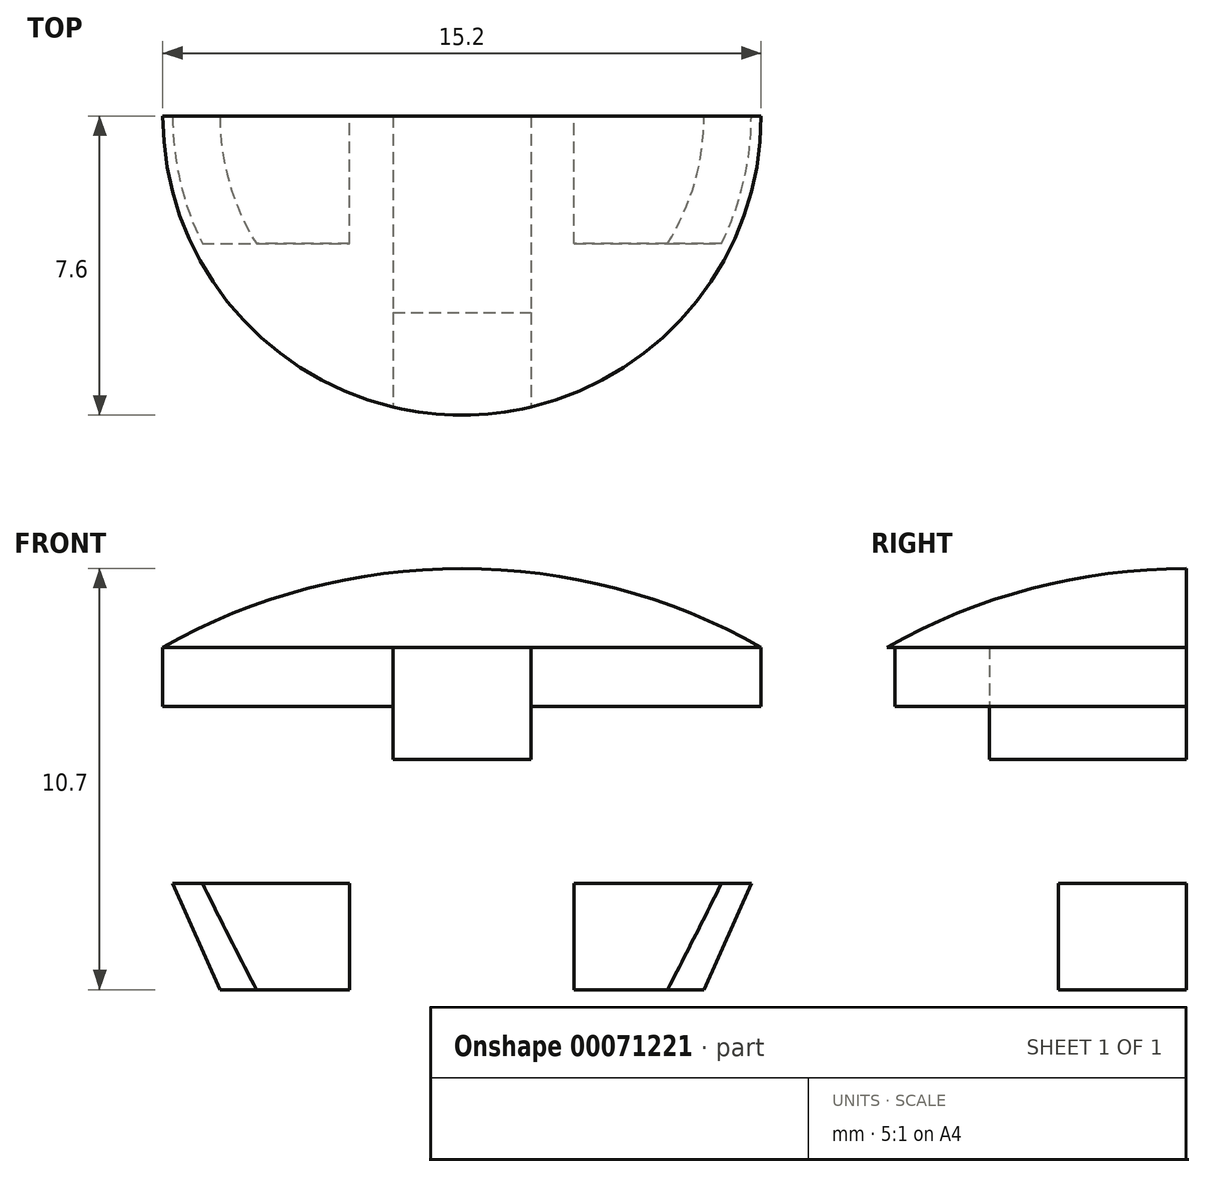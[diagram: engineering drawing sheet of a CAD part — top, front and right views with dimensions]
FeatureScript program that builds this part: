
annotation { "Feature Type Name" : "Feature", "Feature Type Description" : "" }
export const myFeature = defineFeature(function(context is Context, id is Id, definition is map)
    precondition{}
    {
        {
            var Q0;
            Q0=qCreatedBy(makeId("Front.planeOp"),FACE);
            var sketch = newSketch(context, id + "F0", { "sketchPlane" : qUnion([Q0])});
            skLineSegment(sketch, "E0", {"start": v(-7.6, 0) * mm, "end": v(7.6, 0) * mm});
            skLineSegment(sketch, "E1", {"start": v(0, 0) * mm, "end": v(0, 2) * mm});
            skArc(sketch, "E2", {"start": v(7.6, 0) * mm, "mid": v(0, 2) * mm, "end": v(-7.6, 0) * mm});
            skLineSegment(sketch, "E3.top", {"start": v(-7.6, -1.5) * mm, "end": v(7.6, -1.5) * mm});
            skLineSegment(sketch, "E3.left", {"start": v(-7.6, 0) * mm, "end": v(-7.6, -1.5) * mm});
            skLineSegment(sketch, "E3.right", {"start": v(7.6, 0) * mm, "end": v(7.6, -1.5) * mm});
            skLineSegment(sketch, "E4", {"start": v(0, 0) * mm, "end": v(0, -1.5) * mm});
            skLineSegment(sketch, "E5.bottom", {"start": v(-1.75, 0) * mm, "end": v(1.75, 0) * mm});
            skLineSegment(sketch, "E5.top", {"start": v(-1.75, -2.85) * mm, "end": v(1.75, -2.85) * mm});
            skLineSegment(sketch, "E5.left", {"start": v(-1.75, 0) * mm, "end": v(-1.75, -2.85) * mm});
            skLineSegment(sketch, "E5.right", {"start": v(1.75, 0) * mm, "end": v(1.75, -2.85) * mm});
            skLineSegment(sketch, "E6.bottom", {"start": v(2.85, -1.5) * mm, "end": v(5.1, -1.5) * mm});
            skLineSegment(sketch, "E6.top", {"start": v(2.85, -8.7) * mm, "end": v(5.1, -8.7) * mm});
            skLineSegment(sketch, "E6.left", {"start": v(2.85, -1.5) * mm, "end": v(2.85, -8.7) * mm});
            skLineSegment(sketch, "E6.right", {"start": v(5.1, -1.5) * mm, "end": v(5.1, -8.7) * mm});
            skLineSegment(sketch, "E7", {"start": v(5.1, -6) * mm, "end": v(7.35, -6) * mm});
            skLineSegment(sketch, "E8", {"start": v(7.35, -6) * mm, "end": v(6.15, -8.7) * mm});
            skLineSegment(sketch, "E9", {"start": v(6.15, -8.7) * mm, "end": v(5.1, -8.7) * mm});
            skLineSegment(sketch, "E10.MirrorCS", {"start": v(-2.85, -1.5) * mm, "end": v(-5.1, -1.5) * mm});
            skLineSegment(sketch, "E11.MirrorCS", {"start": v(-2.85, -1.5) * mm, "end": v(-2.85, -8.7) * mm});
            skLineSegment(sketch, "E12.MirrorCS", {"start": v(-5.1, -1.5) * mm, "end": v(-5.1, -8.7) * mm});
            skLineSegment(sketch, "E13.MirrorCS", {"start": v(-2.85, -8.7) * mm, "end": v(-5.1, -8.7) * mm});
            skLineSegment(sketch, "E14.MirrorCS", {"start": v(-6.15, -8.7) * mm, "end": v(-5.1, -8.7) * mm});
            skLineSegment(sketch, "E15.MirrorCS", {"start": v(-7.35, -6) * mm, "end": v(-6.15, -8.7) * mm});
            skLineSegment(sketch, "E16.MirrorCS", {"start": v(-5.1, -6) * mm, "end": v(-7.35, -6) * mm});
            skLineSegment(sketch, "E17", {"start": v(5.1, -6) * mm, "end": v(2.85, -6) * mm});
            skLineSegment(sketch, "E18.MirrorCS", {"start": v(-5.1, -6) * mm, "end": v(-2.85, -6) * mm});
            skSolve(sketch);
        }
        {
            var Q0;
            {var subQ0=sQuery(id+"F0.wireOp",EDGE,"E3.left");Q0=makeQuery(id+"F0.imprint","IMPRINT",FACE,{"disambiguationData":[TD([[makeQuery(id+"F0.imprint","IMPRINT",EDGE,{"derivedFrom":subQ0}),1.0]])]});}
            var Q1;
            {var subQ0=sQuery(id+"F0.wireOp",EDGE,"E1");Q1=makeQuery(id+"F0.imprint","IMPRINT",FACE,{"disambiguationData":[TD([[makeQuery(id+"F0.imprint","IMPRINT",EDGE,{"derivedFrom":subQ0}),1.0]])]});}
            var Q2;
            {var subQ0=sQuery(id+"F0.wireOp",EDGE,"E4");Q2=makeQuery(id+"F0.imprint","IMPRINT",FACE,{"disambiguationData":[TD([[makeQuery(id+"F0.imprint","IMPRINT",EDGE,{"derivedFrom":subQ0}),-1.0]])]});}
            var Q3;
            Q3=sQuery(id+"F0.wireOp",EDGE,"E1");
            revolve(context, id + "F1", {"entities" : qUnion([Q0, Q1, Q2]), "axis" : qUnion([Q3]), "revolveType" : RevolveType.FULL});
        }
        {
            var Q0;
            {var subQ0=sQuery(id+"F0.wireOp",EDGE,"E10.MirrorCS");Q0=makeQuery(id+"F0.imprint","IMPRINT",FACE,{"disambiguationData":[TD([[makeQuery(id+"F0.imprint","IMPRINT",EDGE,{"derivedFrom":subQ0}),1.0]])]});}
            var Q1;
            {var subQ0=sQuery(id+"F0.wireOp",EDGE,"E13.MirrorCS");Q1=makeQuery(id+"F0.imprint","IMPRINT",FACE,{"disambiguationData":[TD([[makeQuery(id+"F0.imprint","IMPRINT",EDGE,{"derivedFrom":subQ0}),-1.0]])]});}
            var Q2;
            {var subQ0=sQuery(id+"F0.wireOp",EDGE,"E6.top");Q2=makeQuery(id+"F0.imprint","IMPRINT",FACE,{"disambiguationData":[TD([[makeQuery(id+"F0.imprint","IMPRINT",EDGE,{"derivedFrom":subQ0}),1.0]])]});}
            var Q3;
            {var subQ0=sQuery(id+"F0.wireOp",EDGE,"E6.bottom");Q3=makeQuery(id+"F0.imprint","IMPRINT",FACE,{"disambiguationData":[TD([[makeQuery(id+"F0.imprint","IMPRINT",EDGE,{"derivedFrom":subQ0}),-1.0]])]});}
            extrude(context, id + "F2", {"entities" : qUnion([Q0, Q1, Q2, Q3]), "operationType" : NewBodyOperationType.ADD, "endBound" : BoundingType.SYMMETRIC, "depth" : 6.5 * mm});
        }
        {
            var Q0;
            {var subQ0=sQuery(id+"F0.wireOp",EDGE,"E14.MirrorCS");Q0=makeQuery(id+"F0.imprint","IMPRINT",FACE,{"disambiguationData":[TD([[makeQuery(id+"F0.imprint","IMPRINT",EDGE,{"derivedFrom":subQ0}),1.0]])]});}
            var Q1;
            {var subQ2=sQuery(id+"F0.wireOp",EDGE,"E7");Q1=makeQuery(id+"F0.imprint","IMPRINT",FACE,{"disambiguationData":[TD([[makeQuery(id+"F0.imprint","IMPRINT",EDGE,{"derivedFrom":subQ2}),-1.0]])]});}
            var Q2;
            Q2=sQuery(id+"F0.wireOp",EDGE,"E1");
            revolve(context, id + "F3", {"operationType" : NewBodyOperationType.ADD, "entities" : qUnion([Q0, Q1]), "axis" : qUnion([Q2]), "revolveType" : RevolveType.SYMMETRIC, "angle" : 70 * degree});
        }
        {
            var Q0;
            {var subQ0=sQuery(id+"F0.wireOp",EDGE,"E4");Q0=makeQuery(id+"F0.imprint","IMPRINT",FACE,{"disambiguationData":[TD([[makeQuery(id+"F0.imprint","IMPRINT",EDGE,{"derivedFrom":subQ0}),-1.0]])]});}
            var Q1;
            {var subQ0=sQuery(id+"F0.wireOp",EDGE,"E4");Q1=makeQuery(id+"F0.imprint","IMPRINT",FACE,{"disambiguationData":[TD([[makeQuery(id+"F0.imprint","IMPRINT",EDGE,{"derivedFrom":subQ0}),1.0]])]});}
            extrude(context, id + "F4", {"entities" : qUnion([Q0, Q1]), "operationType" : NewBodyOperationType.REMOVE, "endBound" : BoundingType.SYMMETRIC, "oppositeDirection" : true, "depth" : 25 * mm});
        }
        {
            var Q0;
            {var subQ1=sQuery(id+"F0.wireOp",EDGE,"E5.top");Q0=makeQuery(id+"F0.imprint","IMPRINT",FACE,{"disambiguationData":[TD([[makeQuery(id+"F0.imprint","IMPRINT",EDGE,{"derivedFrom":subQ1}),1.0]])]});}
            var Q1;
            {var subQ0=sQuery(id+"F0.wireOp",EDGE,"E4");Q1=makeQuery(id+"F0.imprint","IMPRINT",FACE,{"disambiguationData":[TD([[makeQuery(id+"F0.imprint","IMPRINT",EDGE,{"derivedFrom":subQ0}),-1.0]])]});}
            var Q2;
            {var subQ0=sQuery(id+"F0.wireOp",EDGE,"E4");Q2=makeQuery(id+"F0.imprint","IMPRINT",FACE,{"disambiguationData":[TD([[makeQuery(id+"F0.imprint","IMPRINT",EDGE,{"derivedFrom":subQ0}),1.0]])]});}
            extrude(context, id + "F5", {"entities" : qUnion([Q0, Q1, Q2]), "operationType" : NewBodyOperationType.ADD, "endBound" : BoundingType.SYMMETRIC, "depth" : 10 * mm});
        }
        {
            var Q0;
            {var subQ0=sQuery(id+"F0.wireOp",EDGE,"E14.MirrorCS");Q0=makeQuery(id+"F0.imprint","IMPRINT",FACE,{"disambiguationData":[TD([[makeQuery(id+"F0.imprint","IMPRINT",EDGE,{"derivedFrom":subQ0}),1.0]])]});}
            var Q1;
            {var subQ0=sQuery(id+"F0.wireOp",EDGE,"E13.MirrorCS");Q1=makeQuery(id+"F0.imprint","IMPRINT",FACE,{"disambiguationData":[TD([[makeQuery(id+"F0.imprint","IMPRINT",EDGE,{"derivedFrom":subQ0}),-1.0]])]});}
            var Q2;
            {var subQ0=sQuery(id+"F0.wireOp",EDGE,"E6.top");Q2=makeQuery(id+"F0.imprint","IMPRINT",FACE,{"disambiguationData":[TD([[makeQuery(id+"F0.imprint","IMPRINT",EDGE,{"derivedFrom":subQ0}),1.0]])]});}
            var Q3;
            {var subQ2=sQuery(id+"F0.wireOp",EDGE,"E7");Q3=makeQuery(id+"F0.imprint","IMPRINT",FACE,{"disambiguationData":[TD([[makeQuery(id+"F0.imprint","IMPRINT",EDGE,{"derivedFrom":subQ2}),-1.0]])]});}
            var Q4;
            Q4=makeQuery(id+"F2.opExtrude","CAP_FACE",FACE,{"disambiguationData":[OSD([sQuery(id+"F0.wireOp",EDGE,"E10.MirrorCS"),sQuery(id+"F0.wireOp",EDGE,"E11.MirrorCS"),sQuery(id+"F0.wireOp",EDGE,"E12.MirrorCS"),sQuery(id+"F0.wireOp",EDGE,"E13.MirrorCS")])],"isStart":false});
            extrude(context, id + "F6", {"entities" : qUnion([Q0, Q1, Q2, Q3]), "operationType" : NewBodyOperationType.REMOVE, "endBound" : BoundingType.THROUGH_ALL, "depth" : 25 * mm, "hasSecondDirection" : true, "secondDirectionBound" : SecondDirectionBoundingType.UP_TO_SURFACE, "secondDirectionOppositeDirection" : false, "secondDirectionBoundEntityFace" : qUnion([Q4]), "secondDirectionDepth" : 25 * mm});
        }
        {
            var Q0;
            {var subQ2=sQuery(id+"F0.wireOp",EDGE,"E7");Q0=makeQuery(id+"F0.imprint","IMPRINT",FACE,{"disambiguationData":[TD([[makeQuery(id+"F0.imprint","IMPRINT",EDGE,{"derivedFrom":subQ2}),-1.0]])]});}
            var Q1;
            {var subQ0=sQuery(id+"F0.wireOp",EDGE,"E14.MirrorCS");Q1=makeQuery(id+"F0.imprint","IMPRINT",FACE,{"disambiguationData":[TD([[makeQuery(id+"F0.imprint","IMPRINT",EDGE,{"derivedFrom":subQ0}),1.0]])]});}
            var Q2;
            {var subQ1=sQuery(id+"F0.wireOp",EDGE,"E5.top");Q2=makeQuery(id+"F0.imprint","IMPRINT",FACE,{"disambiguationData":[TD([[makeQuery(id+"F0.imprint","IMPRINT",EDGE,{"derivedFrom":subQ1}),1.0]])]});}
            var Q3;
            {var subQ0=sQuery(id+"F0.wireOp",EDGE,"E6.bottom");Q3=makeQuery(id+"F0.imprint","IMPRINT",FACE,{"disambiguationData":[TD([[makeQuery(id+"F0.imprint","IMPRINT",EDGE,{"derivedFrom":subQ0}),-1.0]])]});}
            var Q4;
            {var subQ0=sQuery(id+"F0.wireOp",EDGE,"E6.top");Q4=makeQuery(id+"F0.imprint","IMPRINT",FACE,{"disambiguationData":[TD([[makeQuery(id+"F0.imprint","IMPRINT",EDGE,{"derivedFrom":subQ0}),1.0]])]});}
            var Q5;
            {var subQ0=sQuery(id+"F0.wireOp",EDGE,"E10.MirrorCS");Q5=makeQuery(id+"F0.imprint","IMPRINT",FACE,{"disambiguationData":[TD([[makeQuery(id+"F0.imprint","IMPRINT",EDGE,{"derivedFrom":subQ0}),1.0]])]});}
            var Q6;
            {var subQ0=sQuery(id+"F0.wireOp",EDGE,"E13.MirrorCS");Q6=makeQuery(id+"F0.imprint","IMPRINT",FACE,{"disambiguationData":[TD([[makeQuery(id+"F0.imprint","IMPRINT",EDGE,{"derivedFrom":subQ0}),-1.0]])]});}
            var Q7;
            {var subQ0=sQuery(id+"F0.wireOp",EDGE,"E1");Q7=makeQuery(id+"F0.imprint","IMPRINT",FACE,{"disambiguationData":[TD([[makeQuery(id+"F0.imprint","IMPRINT",EDGE,{"derivedFrom":subQ0}),-1.0]])]});}
            var Q8;
            {var subQ0=sQuery(id+"F0.wireOp",EDGE,"E1");Q8=makeQuery(id+"F0.imprint","IMPRINT",FACE,{"disambiguationData":[TD([[makeQuery(id+"F0.imprint","IMPRINT",EDGE,{"derivedFrom":subQ0}),1.0]])]});}
            var Q9;
            {var subQ0=sQuery(id+"F0.wireOp",EDGE,"E3.left");Q9=makeQuery(id+"F0.imprint","IMPRINT",FACE,{"disambiguationData":[TD([[makeQuery(id+"F0.imprint","IMPRINT",EDGE,{"derivedFrom":subQ0}),1.0]])]});}
            var Q10;
            {var subQ0=sQuery(id+"F0.wireOp",EDGE,"E3.right");Q10=makeQuery(id+"F0.imprint","IMPRINT",FACE,{"disambiguationData":[TD([[makeQuery(id+"F0.imprint","IMPRINT",EDGE,{"derivedFrom":subQ0}),-1.0]])]});}
            var Q11;
            {var subQ0=sQuery(id+"F0.wireOp",EDGE,"E4");Q11=makeQuery(id+"F0.imprint","IMPRINT",FACE,{"disambiguationData":[TD([[makeQuery(id+"F0.imprint","IMPRINT",EDGE,{"derivedFrom":subQ0}),-1.0]])]});}
            var Q12;
            {var subQ0=sQuery(id+"F0.wireOp",EDGE,"E4");Q12=makeQuery(id+"F0.imprint","IMPRINT",FACE,{"disambiguationData":[TD([[makeQuery(id+"F0.imprint","IMPRINT",EDGE,{"derivedFrom":subQ0}),1.0]])]});}
            extrude(context, id + "F7", {"entities" : qUnion([Q0, Q1, Q2, Q3, Q4, Q5, Q6, Q7, Q8, Q9, Q10, Q11, Q12]), "operationType" : NewBodyOperationType.REMOVE, "endBound" : BoundingType.THROUGH_ALL, "oppositeDirection" : true, "depth" : 25 * mm});
        }
    });
